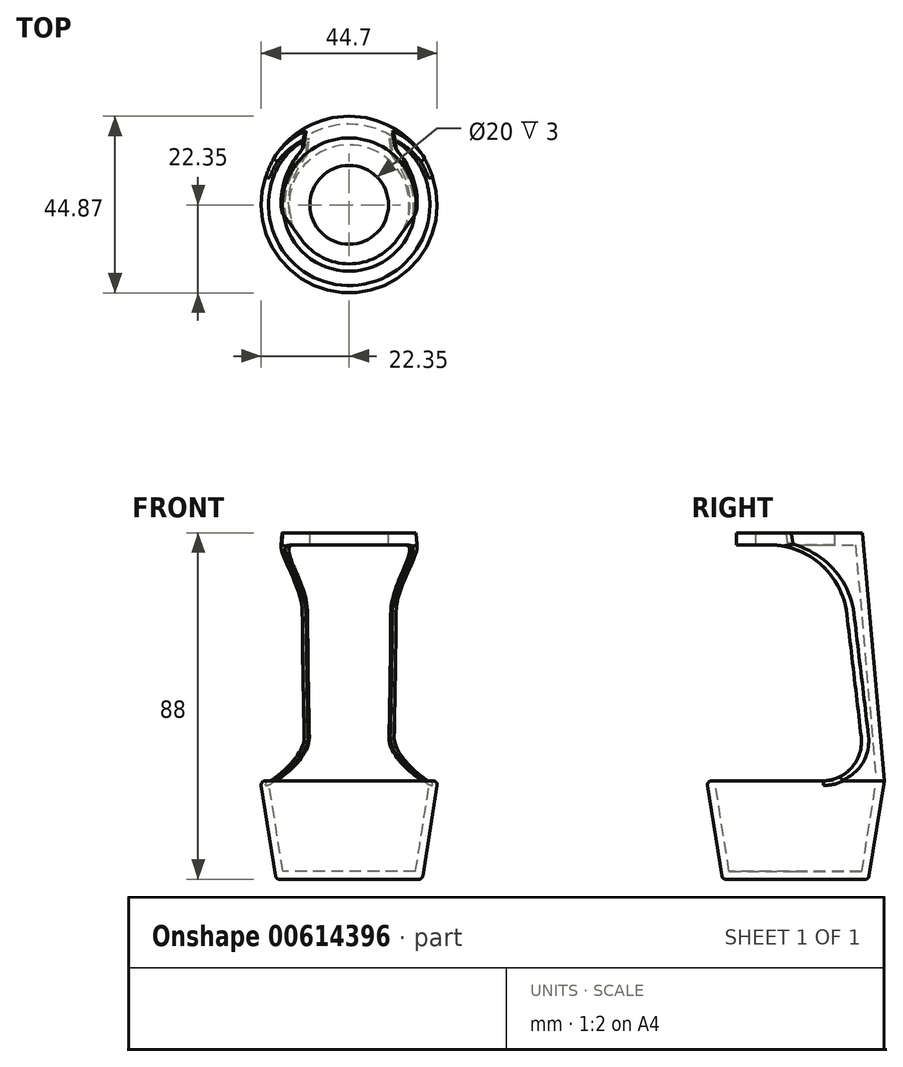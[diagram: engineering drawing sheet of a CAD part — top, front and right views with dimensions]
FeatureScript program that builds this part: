
annotation { "Feature Type Name" : "Feature", "Feature Type Description" : "" }
export const myFeature = defineFeature(function(context is Context, id is Id, definition is map)
    precondition{}
    {
        {
            var Q0;
            Q0=qCreatedBy(makeId("Front.planeOp"),FACE);
            var sketch = newSketch(context, id + "F0", { "sketchPlane" : qUnion([Q0])});
            skLineSegment(sketch, "E0", {"start": v(0, 60) * mm, "end": v(0, 0) * mm, "construction": true});
            skLineSegment(sketch, "E1", {"start": v(0, 60) * mm, "end": v(0, 63) * mm});
            skLineSegment(sketch, "E2", {"start": v(0, 63) * mm, "end": v(17, 63) * mm});
            skLineSegment(sketch, "E3", {"start": v(17, 63) * mm, "end": v(22.52, 0) * mm});
            skLineSegment(sketch, "E4", {"start": v(22.52, 0) * mm, "end": v(18.57, -25) * mm});
            skLineSegment(sketch, "E5", {"start": v(18.57, -25) * mm, "end": v(0, -25) * mm});
            skLineSegment(sketch, "E6", {"start": v(0, 60) * mm, "end": v(15.24, 60) * mm});
            skLineSegment(sketch, "E7", {"start": v(15.24, 60) * mm, "end": v(20.5, 0) * mm});
            skLineSegment(sketch, "E8", {"start": v(20.5, 0) * mm, "end": v(16.86, -23) * mm});
            skLineSegment(sketch, "E9", {"start": v(16.86, -23) * mm, "end": v(0, -23) * mm});
            skLineSegment(sketch, "E10", {"start": v(0, -25) * mm, "end": v(0, -23) * mm});
            skSolve(sketch);
        }
        {
            var Q0;
            Q0=makeQuery(id+"F0.imprint","IMPRINT",FACE,{"disambiguationData":[TD([[makeQuery(id+"F0.imprint","IMPRINT",EDGE,{"derivedFrom":sQuery(id+"F0.wireOp",EDGE,"E1")}),-1.0]])]});
            var Q1;
            Q1=sQuery(id+"F0.wireOp",EDGE,"E0");
            revolve(context, id + "F1", {"entities" : qUnion([Q0]), "axis" : qUnion([Q1]), "revolveType" : RevolveType.FULL});
        }
        {
            var Q0;
            Q0=qCreatedBy(makeId("Front.planeOp"),FACE);
            var sketch = newSketch(context, id + "F2", { "sketchPlane" : qUnion([Q0])});
            skLineSegment(sketch, "E11.0", {"start": v(15.24, 60) * mm, "end": v(20.5, 0) * mm});
            skLineSegment(sketch, "E12.0", {"start": v(17.26, 60) * mm, "end": v(22.52, 0) * mm});
            skLineSegment(sketch, "E13", {"start": v(20.5, 0) * mm, "end": v(22.52, 0) * mm});
            skLineSegment(sketch, "E14", {"start": v(15.24, 60) * mm, "end": v(17.26, 60) * mm});
            skPoint(sketch, "E15.orphan", {"position": v(17, 63) * mm});
            skSolve(sketch);
        }
        {
            var Q0;
            Q0=qSketchRegion(id+"F2",true);
            var Q1;
            Q1=sQuery(id+"F0.wireOp",EDGE,"E0");
            revolve(context, id + "F3", {"operationType" : NewBodyOperationType.REMOVE, "entities" : qUnion([Q0]), "axis" : qUnion([Q1]), "revolveType" : RevolveType.ONE_DIRECTION, "angle" : 180 * degree});
        }
        {
            var Q0;
            Q0=qCreatedBy(makeId("Right.planeOp"),FACE);
            var sketch = newSketch(context, id + "F4", { "sketchPlane" : qUnion([Q0])});
            skLineSegment(sketch, "E16", {"start": v(0, 60) * mm, "end": v(11, 60) * mm});
            skLineSegment(sketch, "E17", {"start": v(0, 60) * mm, "end": v(0, 0) * mm});
            skLineSegment(sketch, "E18", {"start": v(0, 0) * mm, "end": v(18, 0) * mm});
            skLineSegment(sketch, "E19", {"start": v(18, 0) * mm, "end": v(11, 60) * mm});
            skSolve(sketch);
        }
        {
            var Q0;
            Q0=qSketchRegion(id+"F4",true);
            extrude(context, id + "F5", {"entities" : qUnion([Q0]), "operationType" : NewBodyOperationType.REMOVE, "endBound" : BoundingType.SYMMETRIC, "depth" : 55 * mm});
        }
        {
            var Q0;
            Q0=makeQuery(id+"F5.boolean.opBoolean","COPY",EDGE,{"disambiguationData":[OD(1.0)],"derivedFrom":makeQuery(id+"F5.opExtrude","SWEPT_EDGE",EDGE,{"disambiguationData":[OSD([sQuery(id+"F4.wireOp",EDGE,"E18"),sQuery(id+"F4.wireOp",EDGE,"E19")])]})});
            var Q1;
            Q1=makeQuery(id+"F5.boolean.opBoolean","COPY",EDGE,{"disambiguationData":[OD(0.0)],"derivedFrom":makeQuery(id+"F5.opExtrude","SWEPT_EDGE",EDGE,{"disambiguationData":[OSD([sQuery(id+"F4.wireOp",EDGE,"E18"),sQuery(id+"F4.wireOp",EDGE,"E19")])]})});
            fillet(context, id + "F6", {"entities" : qUnion([Q0, Q1]), "radius" : 10 * mm, "tangentPropagation" : true, "allowEdgeOverflow" : false});
        }
        {
            var Q0;
            Q0=makeQuery(id+"F5.boolean.opBoolean","COPY",EDGE,{"disambiguationData":[OD(1.0)],"derivedFrom":makeQuery(id+"F5.opExtrude","SWEPT_EDGE",EDGE,{"disambiguationData":[OSD([sQuery(id+"F4.wireOp",EDGE,"E16"),sQuery(id+"F4.wireOp",EDGE,"E19")])]})});
            var Q1;
            Q1=makeQuery(id+"F5.boolean.opBoolean","COPY",EDGE,{"disambiguationData":[OD(0.0)],"derivedFrom":makeQuery(id+"F5.opExtrude","SWEPT_EDGE",EDGE,{"disambiguationData":[OSD([sQuery(id+"F4.wireOp",EDGE,"E16"),sQuery(id+"F4.wireOp",EDGE,"E19")])]})});
            fillet(context, id + "F7", {"entities" : qUnion([Q0, Q1]), "radius" : 20 * mm, "tangentPropagation" : true, "allowEdgeOverflow" : false});
        }
        {
            var Q0;
            Q0=makeQuery(id+"F7.opFillet","BLEND_EDGE",EDGE,{"blendedFrom":[makeQuery(id+"F5.boolean.opBoolean","COPY",EDGE,{"disambiguationData":[OD(0.0)],"derivedFrom":makeQuery(id+"F5.opExtrude","SWEPT_EDGE",EDGE,{"disambiguationData":[OSD([sQuery(id+"F4.wireOp",EDGE,"E16"),sQuery(id+"F4.wireOp",EDGE,"E19")])]})}),makeQuery(id+"F1.opRevolve","SWEPT_FACE",FACE,{"disambiguationData":[OSD([sQuery(id+"F0.wireOp",EDGE,"E3")])]})],"blendedInto":[makeQuery(id+"F1.opRevolve","SWEPT_FACE",FACE,{"disambiguationData":[OSD([sQuery(id+"F0.wireOp",EDGE,"E3")])]})]});
            var Q1;
            {var subQ0=makeQuery(id+"F1.opRevolve","SWEPT_EDGE",EDGE,{"disambiguationData":[OSD([sQuery(id+"F0.wireOp",EDGE,"E3"),sQuery(id+"F0.wireOp",EDGE,"E4")])]});Q1=makeQuery(id+"F5.boolean.opBoolean","MERGE",EDGE,{"derivedFrom":[makeQuery(id+"F3.boolean.opBoolean","MERGE",EDGE,{"derivedFrom":[subQ0,makeQuery(id+"F3.opRevolve","SWEPT_EDGE",EDGE,{"disambiguationData":[OSD([sQuery(id+"F2.wireOp",EDGE,"E12.0"),sQuery(id+"F2.wireOp",EDGE,"E13")])]})]}),makeQuery(id+"F3.boolean.opBoolean","SPLIT",EDGE,{"derivedFrom":subQ0})]});}
            var Q2;
            Q2=makeQuery(id+"F1.opRevolve","SWEPT_EDGE",EDGE,{"disambiguationData":[OSD([sQuery(id+"F0.wireOp",EDGE,"E4"),sQuery(id+"F0.wireOp",EDGE,"E5")])]});
            fillet(context, id + "F8", {"entities" : qUnion([Q0, Q1, Q2]), "radius" : 1 * mm, "tangentPropagation" : true, "allowEdgeOverflow" : false});
        }
        {
            var Q0;
            Q0=makeQuery(id+"F1.opRevolve","SWEPT_FACE",FACE,{"disambiguationData":[OSD([sQuery(id+"F0.wireOp",EDGE,"E2")])]});
            var sketch = newSketch(context, id + "F9", { "sketchPlane" : qUnion([Q0])});
            skCircle(sketch, "E20", {"center": v(0, 0) * mm, "radius": 10 * mm});
            skSolve(sketch);
        }
        {
            var Q0;
            Q0=qSketchRegion(id+"F9",true);
            extrude(context, id + "F10", {"entities" : qUnion([Q0]), "operationType" : NewBodyOperationType.REMOVE, "oppositeDirection" : true, "depth" : 5 * mm, "offsetDistance" : 25 * mm});
        }
        {
            var Q0;
            Q0=makeQuery(id+"F1.opRevolve","SWEPT_FACE",FACE,{"disambiguationData":[OSD([sQuery(id+"F0.wireOp",EDGE,"E2")])]});
            var sketch = newSketch(context, id + "F11", { "sketchPlane" : qUnion([Q0])});
            skArc(sketch, "E21", {"start": v(0, -15) * mm, "mid": v(6.8, -13.37) * mm, "end": v(12.14, -8.82) * mm});
            skLineSegment(sketch, "E22", {"start": v(19.7, 1.6) * mm, "end": v(12.14, -8.82) * mm});
            skLineSegment(sketch, "E23", {"start": v(23.24, -18.97) * mm, "end": v(0, -25.63) * mm});
            skLineSegment(sketch, "E24", {"start": v(19.7, 1.6) * mm, "end": v(23.24, -18.97) * mm});
            skLineSegment(sketch, "E25", {"start": v(0, 0) * mm, "end": v(0, -15) * mm, "construction": true});
            skPoint(sketch, "E26.start.orphan", {"position": v(-17, 0) * mm});
            skLineSegment(sketch, "E27.MirrorCS", {"start": v(-23.24, -18.97) * mm, "end": v(0, -25.63) * mm});
            skArc(sketch, "E28.MirrorCS", {"start": v(0, -15) * mm, "mid": v(-6.8, -13.37) * mm, "end": v(-12.14, -8.82) * mm});
            skLineSegment(sketch, "E29.MirrorCS", {"start": v(-19.7, 1.6) * mm, "end": v(-12.14, -8.82) * mm});
            skLineSegment(sketch, "E30.MirrorCS", {"start": v(-19.7, 1.6) * mm, "end": v(-23.24, -18.97) * mm});
            skSolve(sketch);
        }
        {
            var Q0;
            Q0=makeQuery(id+"F11.imprint","IMPRINT",FACE,{"disambiguationData":[TD([[makeQuery(id+"F11.imprint","IMPRINT",EDGE,{"derivedFrom":sQuery(id+"F11.wireOp",EDGE,"E23")}),-1.0]])]});
            var Q1;
            Q1=makeQuery(id+"F11.imprint","IMPRINT",FACE,{"disambiguationData":[TD([[makeQuery(id+"F11.imprint","IMPRINT",EDGE,{"derivedFrom":sQuery(id+"F11.wireOp",EDGE,"E21")}),-1.0]])]});
            extrude(context, id + "F12", {"entities" : qUnion([Q0, Q1]), "operationType" : NewBodyOperationType.REMOVE, "oppositeDirection" : true, "depth" : 15 * mm, "offsetDistance" : 25 * mm});
        }
        {
            var Q0;
            Q0=makeQuery(id+"F12.boolean.opBoolean","INTERSECT",EDGE,{"derivedFrom":[makeQuery(id+"F1.opRevolve","SWEPT_FACE",FACE,{"disambiguationData":[OSD([sQuery(id+"F0.wireOp",EDGE,"E3")])]}),makeQuery(id+"F12.opExtrude","SWEPT_FACE",FACE,{"disambiguationData":[OSD([sQuery(id+"F11.wireOp",EDGE,"E22"),sQuery(id+"F11.wireOp",EDGE,"kLoqPunC-dOfU-TKPz-Pnu8-qVxWjo3u3uOn")])]})]});
            var Q1;
            Q1=makeQuery(id+"F12.boolean.opBoolean","INTERSECT",EDGE,{"derivedFrom":[makeQuery(id+"F1.opRevolve","SWEPT_FACE",FACE,{"disambiguationData":[OSD([sQuery(id+"F0.wireOp",EDGE,"E3")])]}),makeQuery(id+"F12.opExtrude","SWEPT_FACE",FACE,{"disambiguationData":[OSD([sQuery(id+"F11.wireOp",EDGE,"E26"),sQuery(id+"F11.wireOp",EDGE,"R9R19m8k-B3BH-idtR-Ydt9-WVIZm6Ay6TTq")])]})]});
            fillet(context, id + "F13", {"entities" : qUnion([Q0, Q1]), "radius" : 4 * mm, "allowEdgeOverflow" : false});
        }
    });
